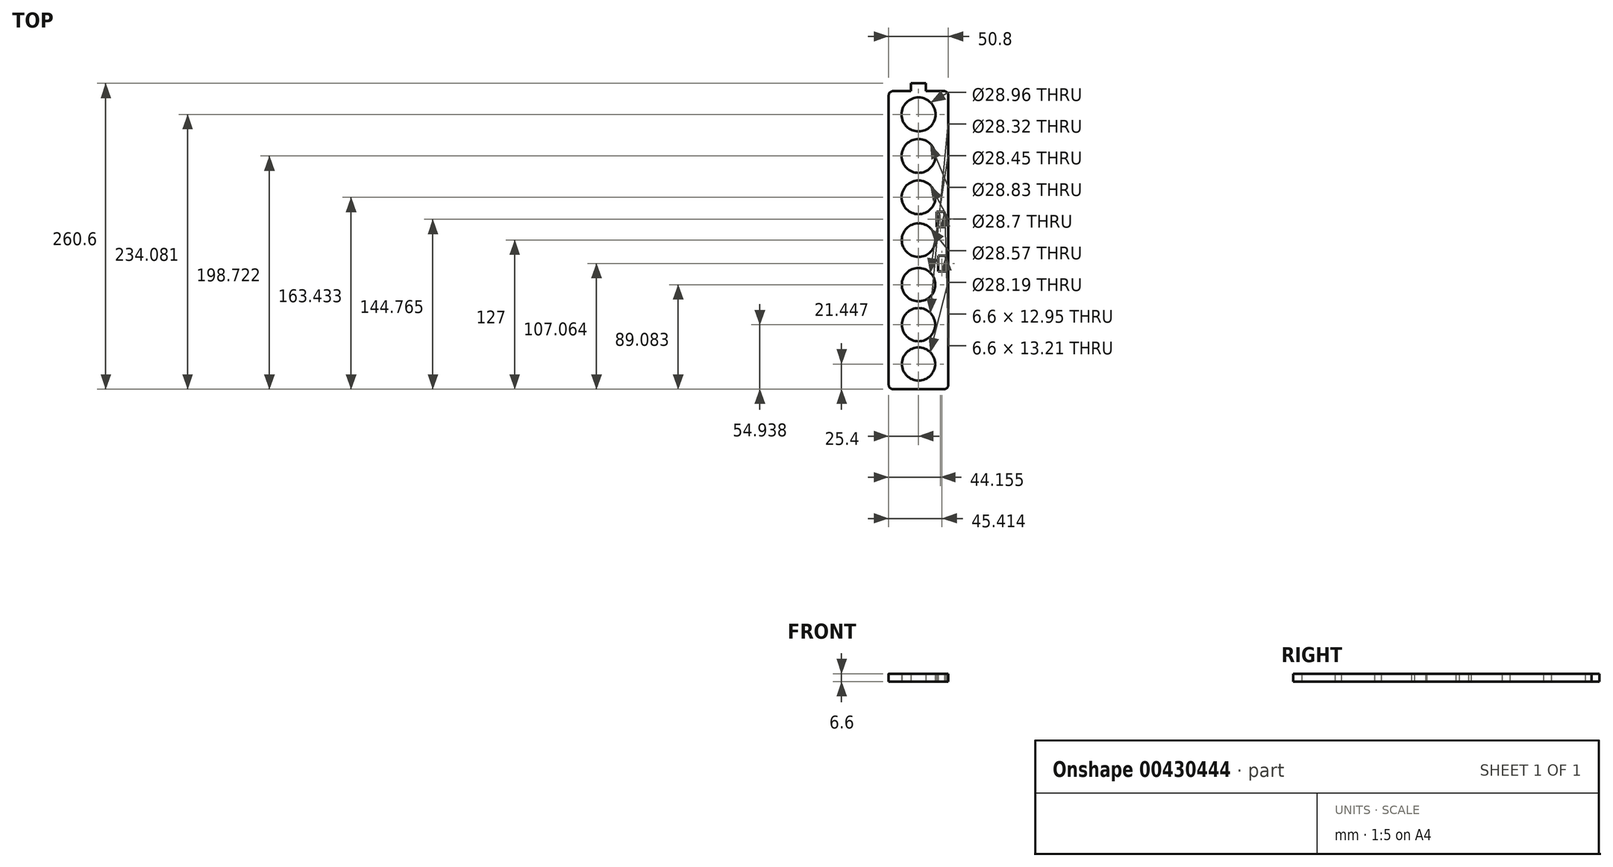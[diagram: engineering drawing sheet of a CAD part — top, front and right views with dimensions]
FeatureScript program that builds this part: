
annotation { "Feature Type Name" : "Feature", "Feature Type Description" : "" }
export const myFeature = defineFeature(function(context is Context, id is Id, definition is map)
    precondition{}
    {
        {
            var Q0;
            Q0=qCreatedBy(makeId("Top.planeOp"),FACE);
            var sketch = newSketch(context, id + "F0", { "sketchPlane" : qUnion([Q0])});
            skLineSegment(sketch, "E0.bottom", {"start": v(21.6, 127) * mm, "end": v(6.24, 127) * mm});
            skLineSegment(sketch, "E0.top", {"start": v(21.59, -127) * mm, "end": v(-21.6, -127) * mm});
            skLineSegment(sketch, "E0.left", {"start": v(25.4, 123.2) * mm, "end": v(25.4, -123.19) * mm});
            skLineSegment(sketch, "E0.right", {"start": v(-25.4, 123.2) * mm, "end": v(-25.4, -123.19) * mm});
            skPoint(sketch, "E0.middle", {"position": v(0, 0) * mm});
            skCircle(sketch, "E1", {"center": v(0, 0) * mm, "radius": 14.29 * mm});
            skCircle(sketch, "E2", {"center": v(0, 36.43) * mm, "radius": 14.35 * mm});
            skCircle(sketch, "E3", {"center": v(0, 71.72) * mm, "radius": 14.41 * mm});
            skCircle(sketch, "E4", {"center": v(0, -37.92) * mm, "radius": 14.22 * mm});
            skCircle(sketch, "E5", {"center": v(0, -72.06) * mm, "radius": 14.16 * mm});
            skCircle(sketch, "E6", {"center": v(0, 107.08) * mm, "radius": 14.48 * mm});
            skCircle(sketch, "E7", {"center": v(0, -105.55) * mm, "radius": 14.1 * mm});
            skPoint(sketch, "E8.visualSharp", {"position": v(-25.4, -127) * mm});
            skArc(sketch, "E8.filletArc", {"start": v(-25.4, -123.19) * mm, "mid": v(-24.28, -125.88) * mm, "end": v(-21.6, -127) * mm});
            skPoint(sketch, "E9.visualSharp", {"position": v(25.4, -127) * mm});
            skArc(sketch, "E9.filletArc", {"start": v(21.59, -127) * mm, "mid": v(24.28, -125.88) * mm, "end": v(25.4, -123.19) * mm});
            skPoint(sketch, "E10.visualSharp", {"position": v(25.4, 127) * mm});
            skArc(sketch, "E10.filletArc", {"start": v(25.4, 123.2) * mm, "mid": v(24.28, 125.88) * mm, "end": v(21.6, 127) * mm});
            skPoint(sketch, "E11.visualSharp", {"position": v(-25.4, 127) * mm});
            skArc(sketch, "E11.filletArc", {"start": v(-21.6, 127) * mm, "mid": v(-24.28, 125.88) * mm, "end": v(-25.4, 123.2) * mm});
            skLineSegment(sketch, "E12.top", {"start": v(-6.46, 133.6) * mm, "end": v(6.24, 133.6) * mm});
            skLineSegment(sketch, "E12.left", {"start": v(-6.46, 127) * mm, "end": v(-6.46, 133.6) * mm});
            skLineSegment(sketch, "E12.right", {"start": v(6.24, 127) * mm, "end": v(6.24, 133.6) * mm});
            skLineSegment(sketch, "E13.bottom", {"start": v(15.45, 24.24) * mm, "end": v(22.06, 24.24) * mm});
            skLineSegment(sketch, "E13.top", {"start": v(15.45, 11.29) * mm, "end": v(22.06, 11.29) * mm});
            skLineSegment(sketch, "E13.left", {"start": v(15.45, 24.24) * mm, "end": v(15.45, 11.29) * mm});
            skLineSegment(sketch, "E13.right", {"start": v(22.06, 24.24) * mm, "end": v(22.06, 11.29) * mm});
            skLineSegment(sketch, "E14.trimOffspring", {"start": v(-6.46, 127) * mm, "end": v(-21.6, 127) * mm});
            skLineSegment(sketch, "E15.bottom", {"start": v(16.71, -13.33) * mm, "end": v(23.32, -13.33) * mm});
            skLineSegment(sketch, "E15.top", {"start": v(16.71, -26.54) * mm, "end": v(23.32, -26.54) * mm});
            skLineSegment(sketch, "E15.left", {"start": v(16.71, -13.33) * mm, "end": v(16.71, -26.54) * mm});
            skLineSegment(sketch, "E15.right", {"start": v(23.32, -13.33) * mm, "end": v(23.32, -26.54) * mm});
            skSolve(sketch);
        }
        {
            var Q0;
            Q0=makeQuery(id+"F0.imprint","IMPRINT",FACE,{"disambiguationData":[TD([[makeQuery(id+"F0.imprint","IMPRINT",EDGE,{"derivedFrom":sQuery(id+"F0.wireOp",EDGE,"E0.bottom")}),1.0]])]});
            extrude(context, id + "F1", {"entities" : qUnion([Q0]), "depth" : 6.6 * mm});
        }
    });
